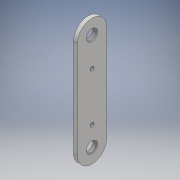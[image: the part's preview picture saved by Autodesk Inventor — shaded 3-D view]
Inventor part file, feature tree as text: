
AUTODESK INVENTOR PART (.ipt)
format: ipt  version: 2018 (Build 220112000, 112)  size: 126,464 bytes
history: native  units: mm
features: hole x2, extrude x1, sketch x1
ambient origin geometry x8: Origin, YZ Plane, XZ Plane, XY Plane, X Axis, Y Axis, Z Axis, Center Point
bodies: Body1 (feature_tree)
feature tree (4):
  extrude  "Extrusion6"  Depth=0.8mm
  hole  "Hole4"  [1 undecoded]
  hole  "Hole5"  [1 undecoded]
  sketch  "Sketch1"  dims[d6=15.0mm d18=100.0mm d40=10.0mm d50=0.0mm d51=0.0mm d52=20.0mm d53=30.0mm d54=4.0mm d55=4.0mm d56=0.0mm d57=10.0mm d58=10.0mm d59=11.6mm d60=6.0mm d61=4.0mm d62=2.0mm d63=90.0deg d64=0.8mm d65=20.594885mm d66=10.0mm d78=10.0mm d79=10.0mm d69=11.6mm d70=6.0mm d71=4.0mm d72=2.0mm d73=90.0deg d74=0.8mm d75=0.0mm]
note: 2 required parameter values undecoded (feature->parameter linkage not recoverable at this tier; creation-order binding heuristic only, values carry confidence <= 0.55)
